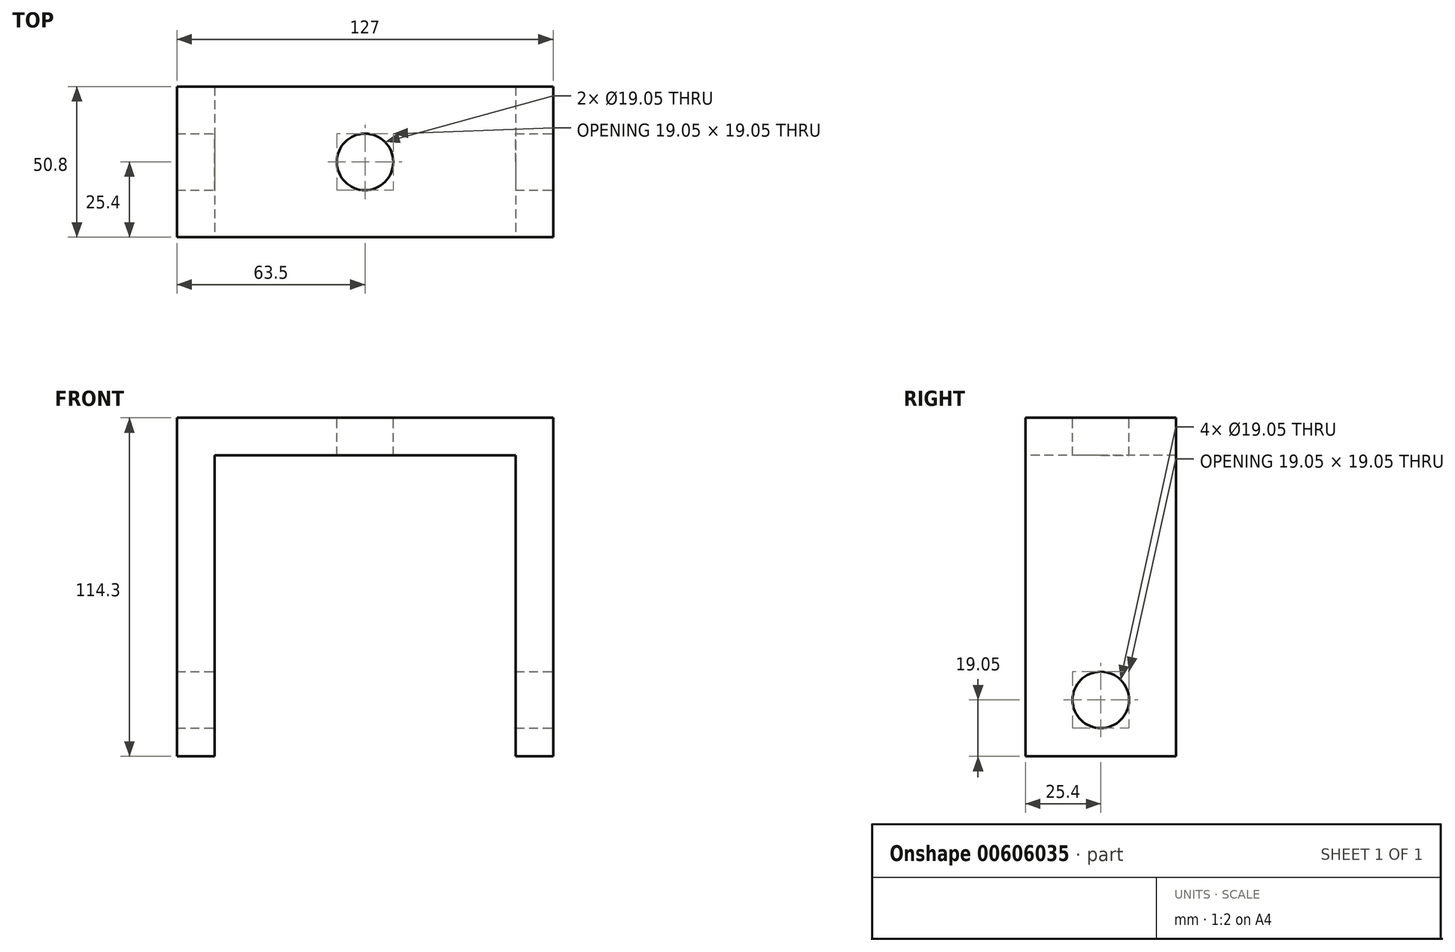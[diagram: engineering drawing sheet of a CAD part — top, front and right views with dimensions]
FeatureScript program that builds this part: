
annotation { "Feature Type Name" : "Feature", "Feature Type Description" : "" }
export const myFeature = defineFeature(function(context is Context, id is Id, definition is map)
    precondition{}
    {
        {
            var Q0;
            Q0=qCreatedBy(makeId("Front.planeOp"),FACE);
            var sketch = newSketch(context, id + "F0", { "sketchPlane" : qUnion([Q0])});
            skLineSegment(sketch, "E0", {"start": v(0, 0) * mm, "end": v(0, 101.6) * mm});
            skLineSegment(sketch, "E1", {"start": v(0, 101.6) * mm, "end": v(101.6, 101.6) * mm});
            skLineSegment(sketch, "E2", {"start": v(101.6, 101.6) * mm, "end": v(101.6, 0) * mm});
            skLineSegment(sketch, "E3", {"start": v(101.6, 0) * mm, "end": v(114.3, 0) * mm});
            skLineSegment(sketch, "E4", {"start": v(114.3, 0) * mm, "end": v(114.3, 114.3) * mm});
            skLineSegment(sketch, "E5", {"start": v(114.3, 114.3) * mm, "end": v(-12.7, 114.3) * mm});
            skLineSegment(sketch, "E6", {"start": v(-12.7, 114.3) * mm, "end": v(-12.7, 0) * mm});
            skLineSegment(sketch, "E7", {"start": v(-12.7, 0) * mm, "end": v(0, 0) * mm});
            skSolve(sketch);
        }
        {
            var Q0;
            Q0=makeQuery(id+"F0.imprint","IMPRINT",FACE,{"disambiguationData":[TD([[makeQuery(id+"F0.imprint","IMPRINT",EDGE,{"derivedFrom":sQuery(id+"F0.wireOp",EDGE,"E0")}),1.0]])]});
            extrude(context, id + "F1", {"entities" : qUnion([Q0]), "oppositeDirection" : true, "depth" : 50.8 * mm, "offsetDistance" : 25.4 * mm});
        }
        {
            var Q0;
            Q0=makeQuery(id+"F1.opExtrude","SWEPT_FACE",FACE,{"disambiguationData":[OSD([sQuery(id+"F0.wireOp",EDGE,"E4")])]});
            var sketch = newSketch(context, id + "F2", { "sketchPlane" : qUnion([Q0])});
            skCircle(sketch, "E8", {"center": v(25.4, 19.05) * mm, "radius": 9.53 * mm});
            skSolve(sketch);
        }
        {
            var Q0;
            Q0=makeQuery(id+"F2.imprint","IMPRINT",FACE,{"disambiguationData":[TD([[makeQuery(id+"F2.imprint","IMPRINT",EDGE,{"derivedFrom":sQuery(id+"F2.wireOp",EDGE,"E8")}),1.0]])]});
            extrude(context, id + "F3", {"entities" : qUnion([Q0]), "operationType" : NewBodyOperationType.REMOVE, "oppositeDirection" : true, "depth" : 127 * mm, "offsetDistance" : 25.4 * mm});
        }
        {
            var Q0;
            Q0=makeQuery(id+"F1.opExtrude","SWEPT_FACE",FACE,{"disambiguationData":[OSD([sQuery(id+"F0.wireOp",EDGE,"E5")])]});
            var sketch = newSketch(context, id + "F4", { "sketchPlane" : qUnion([Q0])});
            skCircle(sketch, "E9", {"center": v(50.8, 25.4) * mm, "radius": 9.53 * mm});
            skSolve(sketch);
        }
        {
            var Q0;
            Q0 = qSketchRegion(id + "F4", true);
            extrude(context, id + "F5", {"entities" : qUnion([Q0]), "operationType" : NewBodyOperationType.REMOVE, "endBound" : BoundingType.UP_TO_NEXT, "oppositeDirection" : true, "depth" : 12.7 * mm, "offsetDistance" : 25.4 * mm});
        }
    });
